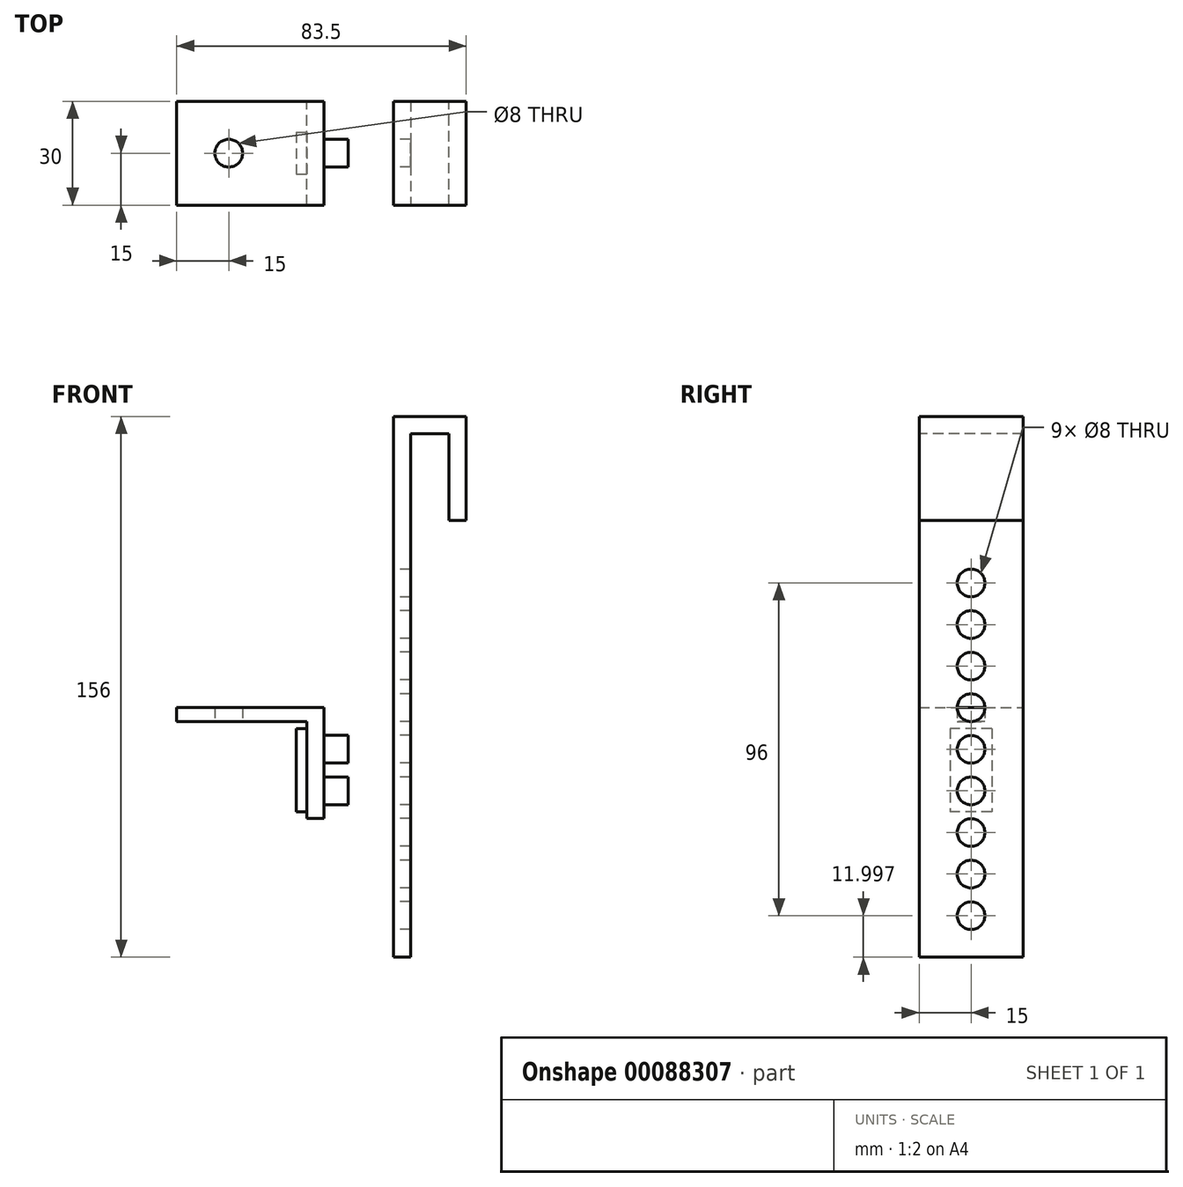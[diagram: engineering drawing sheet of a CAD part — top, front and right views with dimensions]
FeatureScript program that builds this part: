
annotation { "Feature Type Name" : "Feature", "Feature Type Description" : "" }
export const myFeature = defineFeature(function(context is Context, id is Id, definition is map)
    precondition{}
    {
        {
            var Q0;
            Q0=qCreatedBy(makeId("Front.planeOp"),FACE);
            var sketch = newSketch(context, id + "F0", { "sketchPlane" : qUnion([Q0])});
            skLineSegment(sketch, "E0", {"start": v(0, 0) * mm, "end": v(0, 60) * mm});
            skLineSegment(sketch, "E1", {"start": v(0, 60) * mm, "end": v(15, 60) * mm});
            skLineSegment(sketch, "E2", {"start": v(15, 60) * mm, "end": v(15, 40) * mm});
            skLineSegment(sketch, "E3", {"start": v(0, 0) * mm, "end": v(0, -63) * mm});
            skLineSegment(sketch, "E4.1", {"start": v(-3, 63) * mm, "end": v(18, 63) * mm});
            skLineSegment(sketch, "E4.2", {"start": v(-3, 0) * mm, "end": v(-3, 63) * mm});
            skLineSegment(sketch, "E4.3", {"start": v(-3, 0) * mm, "end": v(-3, -100) * mm});
            skLineSegment(sketch, "E5.bottom", {"start": v(15, 40) * mm, "end": v(18, 40) * mm});
            skLineSegment(sketch, "E5.left", {"start": v(15, 40) * mm, "end": v(15, 60) * mm});
            skLineSegment(sketch, "E5.right", {"start": v(18, 40) * mm, "end": v(18, 63) * mm});
            skLineSegment(sketch, "E6.bottom", {"start": v(-3, -100) * mm, "end": v(0, -100) * mm});
            skLineSegment(sketch, "E6.top", {"start": v(-3, -63) * mm, "end": v(0, -63) * mm});
            skLineSegment(sketch, "E6.left", {"start": v(-3, -100) * mm, "end": v(-3, -63) * mm});
            skLineSegment(sketch, "E6.right", {"start": v(0, -100) * mm, "end": v(0, -63) * mm});
            skSolve(sketch);
        }
        {
            var Q0;
            Q0=qCreatedBy(makeId("Right.planeOp"),FACE);
            var sketch = newSketch(context, id + "F1", { "sketchPlane" : qUnion([Q0])});
            skLineSegment(sketch, "E7.0", {"start": v(-15, 66.87) * mm, "end": v(15, 66.87) * mm});
            skLineSegment(sketch, "E8.0", {"start": v(-15, -89.13) * mm, "end": v(-15, 66.87) * mm});
            skLineSegment(sketch, "E9", {"start": v(15, -29.13) * mm, "end": v(-15, -29.13) * mm, "construction": true});
            skLineSegment(sketch, "E10", {"start": v(15, 66.87) * mm, "end": v(15, -29.13) * mm, "construction": true});
            skLineSegment(sketch, "E11", {"start": v(15, 18.87) * mm, "end": v(-15, 18.87) * mm, "construction": true});
            skLineSegment(sketch, "E12", {"start": v(15, 18.87) * mm, "end": v(15, -29.13) * mm, "construction": true});
            skLineSegment(sketch, "E13", {"start": v(15, -5.13) * mm, "end": v(-15, -5.13) * mm, "construction": true});
            skLineSegment(sketch, "E14", {"start": v(15, 18.87) * mm, "end": v(15, -5.13) * mm, "construction": true});
            skLineSegment(sketch, "E15", {"start": v(15, 6.87) * mm, "end": v(-15, 6.87) * mm, "construction": true});
            skLineSegment(sketch, "E16.MirrorCS", {"start": v(15, -17.13) * mm, "end": v(-15, -17.13) * mm, "construction": true});
            skLineSegment(sketch, "E17.MirrorCS", {"start": v(15, -41.13) * mm, "end": v(-15, -41.13) * mm, "construction": true});
            skLineSegment(sketch, "E18.MirrorCS", {"start": v(15, -53.13) * mm, "end": v(-15, -53.13) * mm, "construction": true});
            skLineSegment(sketch, "E19.MirrorCS", {"start": v(15, -65.13) * mm, "end": v(-15, -65.13) * mm, "construction": true});
            skLineSegment(sketch, "E20.MirrorCS", {"start": v(15, -77.13) * mm, "end": v(-15, -77.13) * mm, "construction": true});
            skLineSegment(sketch, "E21.MirrorCS", {"start": v(15, -89.13) * mm, "end": v(-15, -89.13) * mm});
            skLineSegment(sketch, "E22", {"start": v(0, 66.87) * mm, "end": v(0, -125.13) * mm, "construction": true});
            skCircle(sketch, "E23", {"center": v(0, -41.13) * mm, "radius": 4 * mm});
            skCircle(sketch, "E24.MirrorC", {"center": v(0, -17.13) * mm, "radius": 4 * mm});
            skCircle(sketch, "E25.MirrorC", {"center": v(0, 6.87) * mm, "radius": 4 * mm});
            skCircle(sketch, "E26.MirrorC", {"center": v(0, -65.13) * mm, "radius": 4 * mm});
            skCircle(sketch, "E27", {"center": v(0, -29.13) * mm, "radius": 4 * mm});
            skCircle(sketch, "E28.MirrorC", {"center": v(0, -53.13) * mm, "radius": 4 * mm});
            skCircle(sketch, "E29.MirrorC", {"center": v(0, -77.13) * mm, "radius": 4 * mm});
            skCircle(sketch, "E30.MirrorC", {"center": v(0, -5.13) * mm, "radius": 4 * mm});
            skCircle(sketch, "E31.MirrorC", {"center": v(0, 18.87) * mm, "radius": 4 * mm});
            skLineSegment(sketch, "E32.trimOffspring", {"start": v(15, -89.13) * mm, "end": v(15, 66.87) * mm});
            skSolve(sketch);
        }
        {
            var Q0;
            Q0 = qSketchRegion(id + "F1", true);
            extrude(context, id + "F2", {"entities" : qUnion([Q0]), "depth" : 2.5 * mm, "hasSecondDirection" : true, "secondDirectionOppositeDirection" : true, "secondDirectionDepth" : 2.5 * mm});
        }
        {
            var Q0;
            Q0=qCreatedBy(makeId("Front.planeOp"),FACE);
            var sketch = newSketch(context, id + "F3", { "sketchPlane" : qUnion([Q0])});
            skLineSegment(sketch, "E33.0", {"start": v(-2.5, 66.87) * mm, "end": v(2.5, 66.87) * mm});
            skLineSegment(sketch, "E34.0", {"start": v(-2.5, 61.87) * mm, "end": v(-2.5, 66.87) * mm});
            skLineSegment(sketch, "E35.bottom", {"start": v(-2.5, 66.87) * mm, "end": v(18.5, 66.87) * mm});
            skLineSegment(sketch, "E35.top", {"start": v(-2.5, 61.87) * mm, "end": v(13.5, 61.87) * mm});
            skLineSegment(sketch, "E35.left", {"start": v(-2.5, 66.87) * mm, "end": v(-2.5, 61.87) * mm});
            skLineSegment(sketch, "E35.right", {"start": v(18.5, 66.87) * mm, "end": v(18.5, 61.87) * mm});
            skLineSegment(sketch, "E36.bottom", {"start": v(18.5, 66.87) * mm, "end": v(13.5, 66.87) * mm});
            skLineSegment(sketch, "E36.top", {"start": v(18.5, 36.87) * mm, "end": v(13.5, 36.87) * mm});
            skLineSegment(sketch, "E36.left", {"start": v(18.5, 66.87) * mm, "end": v(18.5, 36.87) * mm});
            skLineSegment(sketch, "E36.right", {"start": v(13.5, 61.87) * mm, "end": v(13.5, 36.87) * mm});
            skPoint(sketch, "E37.orphan", {"position": v(-2.5, -55.38) * mm});
            skPoint(sketch, "E38.0.start.orphan", {"position": v(2.5, -75) * mm});
            skLineSegment(sketch, "E39", {"start": v(13.5, 61.87) * mm, "end": v(-2.5, 61.87) * mm});
            skLineSegment(sketch, "E40", {"start": v(2.5, 66.87) * mm, "end": v(13.5, 66.87) * mm});
            skSolve(sketch);
        }
        {
            var Q0;
            Q0 = qSketchRegion(id + "F3", true);
            extrude(context, id + "F4", {"entities" : qUnion([Q0]), "operationType" : NewBodyOperationType.ADD, "depth" : 15 * mm, "hasSecondDirection" : true, "secondDirectionOppositeDirection" : true, "secondDirectionDepth" : 15 * mm});
        }
        {
            var Q0;
            Q0=qCreatedBy(makeId("Right.planeOp"),FACE);
            cPlane(context, id + "F5", {"entities" : qUnion([Q0]), "cplaneType" : CPlaneType.OFFSET, "offset" : 25 * mm, "oppositeDirection" : true, "width" : 150 * mm, "height" : 150 * mm});
        }
        {
            var Q0;
            Q0=qCreatedBy(id+"F5.planeOp",FACE);
            var sketch = newSketch(context, id + "F6", { "sketchPlane" : qUnion([Q0])});
            skCircle(sketch, "E41.0", {"center": v(0, -29.13) * mm, "radius": 4 * mm});
            skCircle(sketch, "E42.0", {"center": v(0, -41.13) * mm, "radius": 4 * mm});
            skLineSegment(sketch, "E43.0", {"start": v(-15, 66.87) * mm, "end": v(-15, 66.87) * mm});
            skCircle(sketch, "E44.0", {"center": v(0, -17.13) * mm, "radius": 4 * mm, "construction": true});
            skCircle(sketch, "E45.0", {"center": v(0, -53.13) * mm, "radius": 4 * mm, "construction": true});
            skLineSegment(sketch, "E46", {"start": v(0, -17.13) * mm, "end": v(-15, -17.13) * mm, "construction": true});
            skLineSegment(sketch, "E47", {"start": v(0, -53.13) * mm, "end": v(-15, -53.13) * mm, "construction": true});
            skLineSegment(sketch, "E48", {"start": v(0, -21.13) * mm, "end": v(-15, -21.13) * mm, "construction": true});
            skLineSegment(sketch, "E49", {"start": v(0, -49.13) * mm, "end": v(-15, -49.13) * mm, "construction": true});
            skLineSegment(sketch, "E50.bottom", {"start": v(-15, -49.13) * mm, "end": v(15, -49.13) * mm});
            skLineSegment(sketch, "E50.top", {"start": v(-15, -17.13) * mm, "end": v(15, -17.13) * mm});
            skLineSegment(sketch, "E50.left", {"start": v(-15, -49.13) * mm, "end": v(-15, -17.13) * mm});
            skLineSegment(sketch, "E50.right", {"start": v(15, -49.13) * mm, "end": v(15, -17.13) * mm});
            skLineSegment(sketch, "E51.top", {"start": v(-15, -21.13) * mm, "end": v(15, -21.13) * mm});
            skLineSegment(sketch, "E51.left", {"start": v(-15, -17.13) * mm, "end": v(-15, -21.13) * mm});
            skLineSegment(sketch, "E51.right", {"start": v(15, -17.13) * mm, "end": v(15, -21.13) * mm});
            skSolve(sketch);
        }
        {
            var Q0;
            Q0 = qSketchRegion(id + "F6", true);
            extrude(context, id + "F7", {"entities" : qUnion([Q0]), "depth" : 2.5 * mm, "hasSecondDirection" : true, "secondDirectionOppositeDirection" : true, "secondDirectionDepth" : 2.5 * mm});
        }
        {
            var Q0;
            Q0=makeQuery(id+"F6.imprint","IMPRINT",FACE,{"disambiguationData":[TD([[makeQuery(id+"F6.imprint","IMPRINT",EDGE,{"derivedFrom":sQuery(id+"F6.wireOp",EDGE,"E50.top")}),-1.0]])]});
            extrude(context, id + "F8", {"entities" : qUnion([Q0]), "operationType" : NewBodyOperationType.ADD, "oppositeDirection" : true, "depth" : 40 * mm});
        }
        {
            var Q0;
            {var subQ0=sQuery(id+"F6.wireOp",EDGE,"E50.top");Q0=makeQuery(id+"F8.boolean.opBoolean","MERGE",FACE,{"derivedFrom":[makeQuery(id+"F7.opExtrude","SWEPT_FACE",FACE,{"disambiguationData":[OSD([subQ0])]}),makeQuery(id+"F8.opExtrude","SWEPT_FACE",FACE,{"disambiguationData":[OSD([subQ0])]})]});}
            var sketch = newSketch(context, id + "F9", { "sketchPlane" : qUnion([Q0])});
            skLineSegment(sketch, "E52.0", {"start": v(-22.5, 15) * mm, "end": v(-65, 15) * mm, "construction": true});
            skLineSegment(sketch, "E53.0", {"start": v(-65, -15) * mm, "end": v(-65, 15) * mm, "construction": true});
            skLineSegment(sketch, "E54.0", {"start": v(-22.5, -15) * mm, "end": v(-65, -15) * mm, "construction": true});
            skLineSegment(sketch, "E55.bottom", {"start": v(-65, 15) * mm, "end": v(-35, 15) * mm, "construction": true});
            skLineSegment(sketch, "E55.top", {"start": v(-65, -15) * mm, "end": v(-35, -15) * mm, "construction": true});
            skLineSegment(sketch, "E55.left", {"start": v(-65, 15) * mm, "end": v(-65, -15) * mm, "construction": true});
            skLineSegment(sketch, "E55.right", {"start": v(-35, 15) * mm, "end": v(-35, -15) * mm, "construction": true});
            skLineSegment(sketch, "E56", {"start": v(-50, 15) * mm, "end": v(-50, -15) * mm, "construction": true});
            skLineSegment(sketch, "E57", {"start": v(-65, 0) * mm, "end": v(-35, 0) * mm, "construction": true});
            skCircle(sketch, "E58", {"center": v(-50, 0) * mm, "radius": 4 * mm});
            skSolve(sketch);
        }
        {
            var Q0;
            Q0 = qSketchRegion(id + "F9", true);
            extrude(context, id + "F10", {"entities" : qUnion([Q0]), "operationType" : NewBodyOperationType.REMOVE, "depth" : 5 * mm, "hasSecondDirection" : true, "secondDirectionOppositeDirection" : true, "secondDirectionDepth" : 5 * mm});
        }
        {
            var Q0;
            Q0=makeQuery(id+"F7.opExtrude","CAP_FACE",FACE,{"disambiguationData":[OSD([sQuery(id+"F6.wireOp",EDGE,"E41.0"),sQuery(id+"F6.wireOp",EDGE,"E42.0"),sQuery(id+"F6.wireOp",EDGE,"E50.bottom"),sQuery(id+"F6.wireOp",EDGE,"E50.left"),sQuery(id+"F6.wireOp",EDGE,"E50.right"),sQuery(id+"F6.wireOp",EDGE,"E50.top"),sQuery(id+"F6.wireOp",EDGE,"E51.left"),sQuery(id+"F6.wireOp",EDGE,"E51.right")])],"isStart":true});
            var sketch = newSketch(context, id + "F11", { "sketchPlane" : qUnion([Q0])});
            skCircle(sketch, "E59", {"center": v(0, -29.13) * mm, "radius": 4 * mm, "construction": true});
            skCircle(sketch, "E60", {"center": v(0, -41.13) * mm, "radius": 4 * mm, "construction": true});
            skLineSegment(sketch, "E61.bottom", {"start": v(-6, -23.13) * mm, "end": v(6, -23.13) * mm});
            skLineSegment(sketch, "E61.top", {"start": v(-6, -47.13) * mm, "end": v(6, -47.13) * mm});
            skLineSegment(sketch, "E61.left", {"start": v(-6, -23.13) * mm, "end": v(-6, -47.13) * mm});
            skLineSegment(sketch, "E61.right", {"start": v(6, -23.13) * mm, "end": v(6, -47.13) * mm});
            skSolve(sketch);
        }
        {
            var Q0;
            Q0 = qSketchRegion(id + "F11", true);
            extrude(context, id + "F12", {"entities" : qUnion([Q0]), "depth" : 3 * mm});
        }
        {
            var Q0;
            Q0=makeQuery(id+"F11.imprint","IMPRINT",FACE,{"disambiguationData":[TD([[makeQuery(id+"F11.imprint","IMPRINT",EDGE,{"derivedFrom":makeQuery(id+"F7.opExtrude","CAP_EDGE",EDGE,{"disambiguationData":[OSD([sQuery(id+"F6.wireOp",EDGE,"E41.0")])],"isStart":true})}),-1.0]])]});
            var Q1;
            Q1=makeQuery(id+"F11.imprint","IMPRINT",FACE,{"disambiguationData":[TD([[makeQuery(id+"F11.imprint","IMPRINT",EDGE,{"derivedFrom":makeQuery(id+"F7.opExtrude","CAP_EDGE",EDGE,{"disambiguationData":[OSD([sQuery(id+"F6.wireOp",EDGE,"E42.0")])],"isStart":true})}),-1.0]])]});
            extrude(context, id + "F13", {"entities" : qUnion([Q0, Q1]), "operationType" : NewBodyOperationType.ADD, "oppositeDirection" : true, "depth" : 12 * mm, "hasSecondDirection" : true, "secondDirectionOppositeDirection" : false, "secondDirectionDepth" : 3 * mm});
        }
    });
